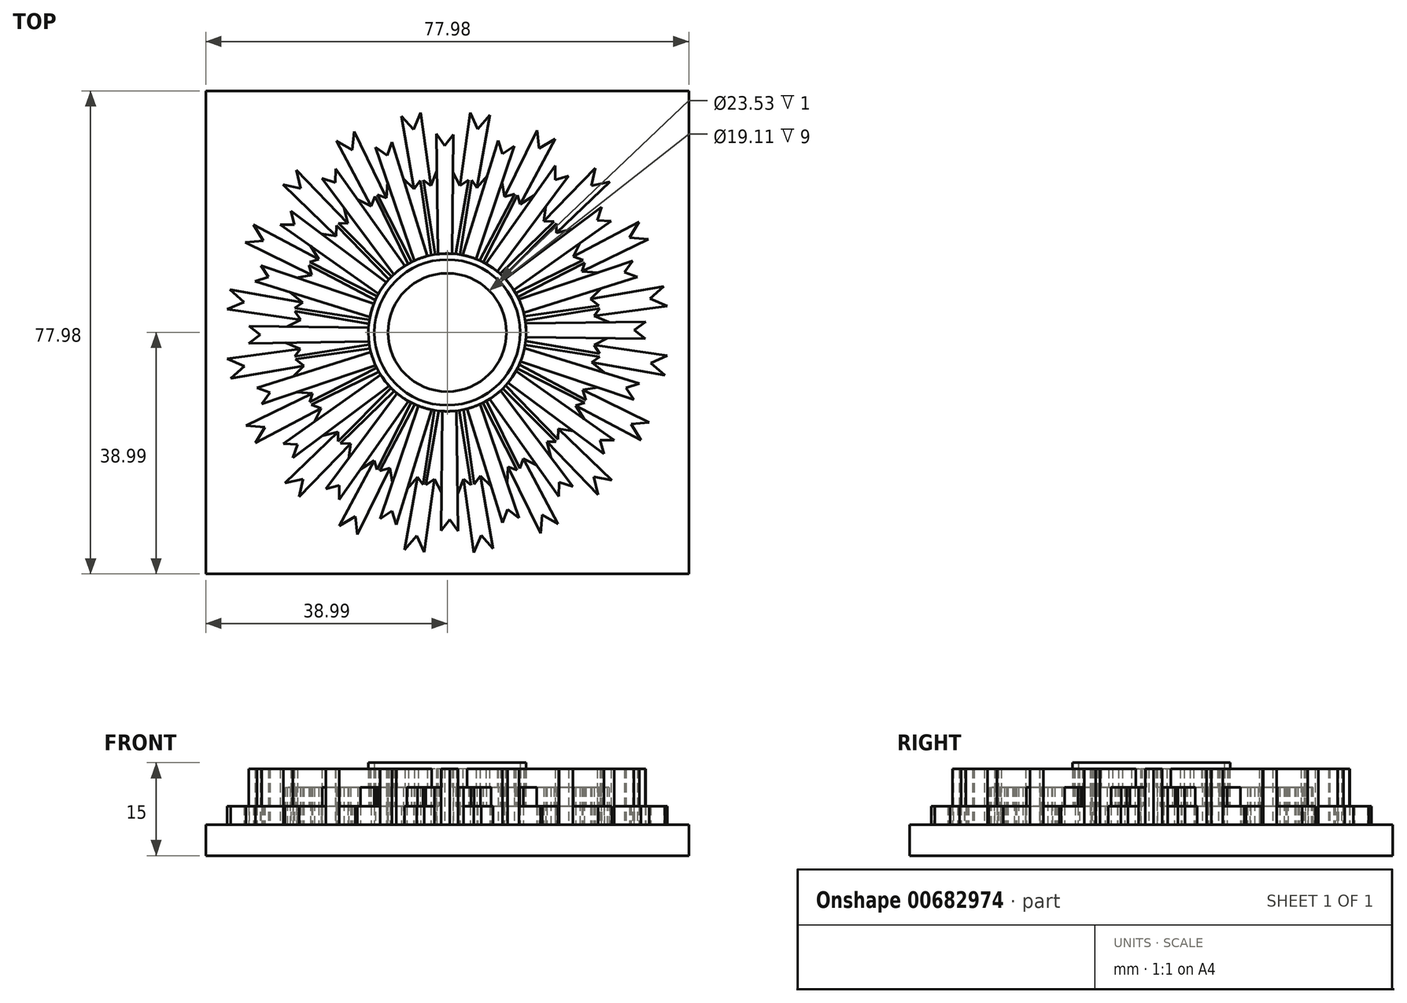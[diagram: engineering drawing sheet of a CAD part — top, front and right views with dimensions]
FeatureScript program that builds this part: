
annotation { "Feature Type Name" : "Feature", "Feature Type Description" : "" }
export const myFeature = defineFeature(function(context is Context, id is Id, definition is map)
    precondition{}
    {
        {
            var Q0;
            Q0=qCreatedBy(makeId("Top.planeOp"),FACE);
            var sketch = newSketch(context, id + "F0", { "sketchPlane" : qUnion([Q0])});
            skCircle(sketch, "E0", {"center": v(0, 0) * mm, "radius": 9.55 * mm});
            skCircle(sketch, "E1", {"center": v(0, 0) * mm, "radius": 11.77 * mm});
            skCircle(sketch, "E2", {"center": v(0, 0) * mm, "radius": 12.74 * mm});
            skLineSegment(sketch, "E3", {"start": v(-8.1, -9.83) * mm, "end": v(-19.6, -25.28) * mm});
            skLineSegment(sketch, "E4", {"start": v(-19.6, -25.28) * mm, "end": v(-17.42, -24.67) * mm});
            skLineSegment(sketch, "E5", {"start": v(-17.42, -24.67) * mm, "end": v(-17.42, -26.96) * mm});
            skLineSegment(sketch, "E6", {"start": v(-17.42, -26.96) * mm, "end": v(-6.24, -11.1) * mm});
            skLineSegment(sketch, "E7.1.0", {"start": v(-8.24, -31.02) * mm, "end": v(-2.5, -12.49) * mm});
            skLineSegment(sketch, "E7.1.1", {"start": v(-8.95, -28.84) * mm, "end": v(-8.24, -31.02) * mm});
            skLineSegment(sketch, "E7.1.2", {"start": v(-10.83, -30.1) * mm, "end": v(-8.95, -28.84) * mm});
            skLineSegment(sketch, "E7.1.3", {"start": v(-4.67, -11.85) * mm, "end": v(-10.83, -30.1) * mm});
            skLineSegment(sketch, "E7.2.0", {"start": v(1.75, -32.05) * mm, "end": v(1.47, -12.65) * mm});
            skLineSegment(sketch, "E7.2.1", {"start": v(0.4, -30.2) * mm, "end": v(1.75, -32.05) * mm});
            skLineSegment(sketch, "E7.2.2", {"start": v(-1, -31.97) * mm, "end": v(0.4, -30.2) * mm});
            skLineSegment(sketch, "E7.2.3", {"start": v(-0.77, -12.71) * mm, "end": v(-1, -31.97) * mm});
            skLineSegment(sketch, "E7.3.0", {"start": v(11.57, -29.94) * mm, "end": v(5.31, -11.58) * mm});
            skLineSegment(sketch, "E7.3.1", {"start": v(9.71, -28.6) * mm, "end": v(11.57, -29.94) * mm});
            skLineSegment(sketch, "E7.3.2", {"start": v(8.93, -30.71) * mm, "end": v(9.71, -28.6) * mm});
            skLineSegment(sketch, "E7.3.3", {"start": v(3.2, -12.33) * mm, "end": v(8.93, -30.71) * mm});
            skLineSegment(sketch, "E7.4.0", {"start": v(20.25, -24.9) * mm, "end": v(8.63, -9.37) * mm});
            skLineSegment(sketch, "E7.4.1", {"start": v(18.08, -24.2) * mm, "end": v(20.25, -24.9) * mm});
            skLineSegment(sketch, "E7.4.2", {"start": v(17.98, -26.45) * mm, "end": v(18.08, -24.2) * mm});
            skLineSegment(sketch, "E7.4.3", {"start": v(6.85, -10.74) * mm, "end": v(17.98, -26.45) * mm});
            skLineSegment(sketch, "E7.5.0", {"start": v(26.96, -17.42) * mm, "end": v(11.1, -6.24) * mm});
            skLineSegment(sketch, "E7.5.1", {"start": v(24.67, -17.42) * mm, "end": v(26.96, -17.42) * mm});
            skLineSegment(sketch, "E7.5.2", {"start": v(25.28, -19.6) * mm, "end": v(24.67, -17.42) * mm});
            skLineSegment(sketch, "E7.5.3", {"start": v(9.83, -8.1) * mm, "end": v(25.28, -19.6) * mm});
            skLineSegment(sketch, "E7.6.0", {"start": v(31.02, -8.24) * mm, "end": v(12.49, -2.5) * mm});
            skLineSegment(sketch, "E7.6.1", {"start": v(28.84, -8.95) * mm, "end": v(31.02, -8.24) * mm});
            skLineSegment(sketch, "E7.6.2", {"start": v(30.1, -10.83) * mm, "end": v(28.84, -8.95) * mm});
            skLineSegment(sketch, "E7.6.3", {"start": v(11.85, -4.67) * mm, "end": v(30.1, -10.83) * mm});
            skLineSegment(sketch, "E7.7.0", {"start": v(32.05, 1.75) * mm, "end": v(12.65, 1.47) * mm});
            skLineSegment(sketch, "E7.7.1", {"start": v(30.2, 0.4) * mm, "end": v(32.05, 1.75) * mm});
            skLineSegment(sketch, "E7.7.2", {"start": v(31.97, -1) * mm, "end": v(30.2, 0.4) * mm});
            skLineSegment(sketch, "E7.7.3", {"start": v(12.71, -0.77) * mm, "end": v(31.97, -1) * mm});
            skLineSegment(sketch, "E7.8.0", {"start": v(29.94, 11.57) * mm, "end": v(11.58, 5.31) * mm});
            skLineSegment(sketch, "E7.8.1", {"start": v(28.6, 9.71) * mm, "end": v(29.94, 11.57) * mm});
            skLineSegment(sketch, "E7.8.2", {"start": v(30.71, 8.93) * mm, "end": v(28.6, 9.71) * mm});
            skLineSegment(sketch, "E7.8.3", {"start": v(12.33, 3.2) * mm, "end": v(30.71, 8.93) * mm});
            skLineSegment(sketch, "E7.9.0", {"start": v(24.9, 20.25) * mm, "end": v(9.37, 8.63) * mm});
            skLineSegment(sketch, "E7.9.1", {"start": v(24.2, 18.08) * mm, "end": v(24.9, 20.25) * mm});
            skLineSegment(sketch, "E7.9.2", {"start": v(26.45, 17.98) * mm, "end": v(24.2, 18.08) * mm});
            skLineSegment(sketch, "E7.9.3", {"start": v(10.74, 6.85) * mm, "end": v(26.45, 17.98) * mm});
            skLineSegment(sketch, "E7.10.0", {"start": v(17.42, 26.96) * mm, "end": v(6.24, 11.1) * mm});
            skLineSegment(sketch, "E7.10.1", {"start": v(17.42, 24.67) * mm, "end": v(17.42, 26.96) * mm});
            skLineSegment(sketch, "E7.10.2", {"start": v(19.6, 25.28) * mm, "end": v(17.42, 24.67) * mm});
            skLineSegment(sketch, "E7.10.3", {"start": v(8.1, 9.83) * mm, "end": v(19.6, 25.28) * mm});
            skLineSegment(sketch, "E7.11.0", {"start": v(8.24, 31.02) * mm, "end": v(2.5, 12.49) * mm});
            skLineSegment(sketch, "E7.11.1", {"start": v(8.95, 28.84) * mm, "end": v(8.24, 31.02) * mm});
            skLineSegment(sketch, "E7.11.2", {"start": v(10.83, 30.1) * mm, "end": v(8.95, 28.84) * mm});
            skLineSegment(sketch, "E7.11.3", {"start": v(4.67, 11.85) * mm, "end": v(10.83, 30.1) * mm});
            skLineSegment(sketch, "E7.12.0", {"start": v(-1.75, 32.05) * mm, "end": v(-1.47, 12.65) * mm});
            skLineSegment(sketch, "E7.12.1", {"start": v(-0.4, 30.2) * mm, "end": v(-1.75, 32.05) * mm});
            skLineSegment(sketch, "E7.12.2", {"start": v(1, 31.97) * mm, "end": v(-0.4, 30.2) * mm});
            skLineSegment(sketch, "E7.12.3", {"start": v(0.77, 12.71) * mm, "end": v(1, 31.97) * mm});
            skLineSegment(sketch, "E7.13.0", {"start": v(-11.57, 29.94) * mm, "end": v(-5.31, 11.58) * mm});
            skLineSegment(sketch, "E7.13.1", {"start": v(-9.71, 28.6) * mm, "end": v(-11.57, 29.94) * mm});
            skLineSegment(sketch, "E7.13.2", {"start": v(-8.93, 30.71) * mm, "end": v(-9.71, 28.6) * mm});
            skLineSegment(sketch, "E7.13.3", {"start": v(-3.2, 12.33) * mm, "end": v(-8.93, 30.71) * mm});
            skLineSegment(sketch, "E7.14.0", {"start": v(-20.25, 24.9) * mm, "end": v(-8.63, 9.37) * mm});
            skLineSegment(sketch, "E7.14.1", {"start": v(-18.08, 24.2) * mm, "end": v(-20.25, 24.9) * mm});
            skLineSegment(sketch, "E7.14.2", {"start": v(-17.98, 26.45) * mm, "end": v(-18.08, 24.2) * mm});
            skLineSegment(sketch, "E7.14.3", {"start": v(-6.85, 10.74) * mm, "end": v(-17.98, 26.45) * mm});
            skLineSegment(sketch, "E7.15.0", {"start": v(-26.96, 17.42) * mm, "end": v(-11.1, 6.24) * mm});
            skLineSegment(sketch, "E7.15.1", {"start": v(-24.67, 17.42) * mm, "end": v(-26.96, 17.42) * mm});
            skLineSegment(sketch, "E7.15.2", {"start": v(-25.28, 19.6) * mm, "end": v(-24.67, 17.42) * mm});
            skLineSegment(sketch, "E7.15.3", {"start": v(-9.83, 8.1) * mm, "end": v(-25.28, 19.6) * mm});
            skLineSegment(sketch, "E7.16.0", {"start": v(-31.02, 8.24) * mm, "end": v(-12.49, 2.5) * mm});
            skLineSegment(sketch, "E7.16.1", {"start": v(-28.84, 8.95) * mm, "end": v(-31.02, 8.24) * mm});
            skLineSegment(sketch, "E7.16.2", {"start": v(-30.1, 10.83) * mm, "end": v(-28.84, 8.95) * mm});
            skLineSegment(sketch, "E7.16.3", {"start": v(-11.85, 4.67) * mm, "end": v(-30.1, 10.83) * mm});
            skLineSegment(sketch, "E7.17.0", {"start": v(-32.05, -1.75) * mm, "end": v(-12.65, -1.47) * mm});
            skLineSegment(sketch, "E7.17.1", {"start": v(-30.2, -0.4) * mm, "end": v(-32.05, -1.75) * mm});
            skLineSegment(sketch, "E7.17.2", {"start": v(-31.97, 1) * mm, "end": v(-30.2, -0.4) * mm});
            skLineSegment(sketch, "E7.17.3", {"start": v(-12.71, 0.77) * mm, "end": v(-31.97, 1) * mm});
            skLineSegment(sketch, "E7.18.0", {"start": v(-29.94, -11.57) * mm, "end": v(-11.58, -5.31) * mm});
            skLineSegment(sketch, "E7.18.1", {"start": v(-28.6, -9.71) * mm, "end": v(-29.94, -11.57) * mm});
            skLineSegment(sketch, "E7.18.2", {"start": v(-30.71, -8.93) * mm, "end": v(-28.6, -9.71) * mm});
            skLineSegment(sketch, "E7.18.3", {"start": v(-12.33, -3.2) * mm, "end": v(-30.71, -8.93) * mm});
            skLineSegment(sketch, "E7.19.0", {"start": v(-24.9, -20.25) * mm, "end": v(-9.37, -8.63) * mm});
            skLineSegment(sketch, "E7.19.1", {"start": v(-24.2, -18.08) * mm, "end": v(-24.9, -20.25) * mm});
            skLineSegment(sketch, "E7.19.2", {"start": v(-26.45, -17.98) * mm, "end": v(-24.2, -18.08) * mm});
            skLineSegment(sketch, "E7.19.3", {"start": v(-10.74, -6.85) * mm, "end": v(-26.45, -17.98) * mm});
            skLineSegment(sketch, "E8", {"start": v(-14, -22.1) * mm, "end": v(-11.8, -20.73) * mm});
            skLineSegment(sketch, "E9", {"start": v(-11.8, -20.73) * mm, "end": v(-11.35, -22.17) * mm});
            skLineSegment(sketch, "E10", {"start": v(-11.35, -22.17) * mm, "end": v(-5.84, -11.32) * mm});
            skLineSegment(sketch, "E11", {"start": v(-5.22, -11.62) * mm, "end": v(-10.89, -22.36) * mm});
            skLineSegment(sketch, "E12", {"start": v(-10.89, -22.36) * mm, "end": v(-9.26, -21.9) * mm});
            skLineSegment(sketch, "E13", {"start": v(-9.26, -21.9) * mm, "end": v(-8.86, -24.28) * mm});
            skLineSegment(sketch, "E14", {"start": v(-11.8, -20.73) * mm, "end": v(-17.42, -31.26) * mm});
            skLineSegment(sketch, "E15", {"start": v(-17.42, -31.26) * mm, "end": v(-14.82, -29.7) * mm});
            skLineSegment(sketch, "E16", {"start": v(-14.82, -29.7) * mm, "end": v(-14.53, -32.63) * mm});
            skLineSegment(sketch, "E17", {"start": v(-14.53, -32.63) * mm, "end": v(-9.26, -21.9) * mm});
            skLineSegment(sketch, "E18.1.0", {"start": v(-6.49, -25.35) * mm, "end": v(-4.81, -23.36) * mm});
            skLineSegment(sketch, "E18.1.1", {"start": v(-4.81, -23.36) * mm, "end": v(-6.91, -35.11) * mm});
            skLineSegment(sketch, "E18.1.2", {"start": v(-4.81, -23.36) * mm, "end": v(-3.94, -24.6) * mm});
            skLineSegment(sketch, "E18.1.3", {"start": v(-3.94, -24.6) * mm, "end": v(-2.05, -12.57) * mm});
            skLineSegment(sketch, "E18.1.4", {"start": v(-3.74, -35.52) * mm, "end": v(-2.04, -23.68) * mm});
            skLineSegment(sketch, "E18.1.5", {"start": v(-3.45, -24.63) * mm, "end": v(-2.04, -23.68) * mm});
            skLineSegment(sketch, "E18.1.6", {"start": v(-1.37, -12.66) * mm, "end": v(-3.45, -24.63) * mm});
            skLineSegment(sketch, "E18.1.7", {"start": v(-2.04, -23.68) * mm, "end": v(-0.93, -25.83) * mm});
            skLineSegment(sketch, "E18.1.8", {"start": v(-4.92, -32.82) * mm, "end": v(-3.74, -35.52) * mm});
            skLineSegment(sketch, "E18.1.9", {"start": v(-6.91, -35.11) * mm, "end": v(-4.92, -32.82) * mm});
            skLineSegment(sketch, "E18.2.0", {"start": v(1.67, -26.11) * mm, "end": v(2.64, -23.7) * mm});
            skLineSegment(sketch, "E18.2.1", {"start": v(2.64, -23.7) * mm, "end": v(4.28, -35.53) * mm});
            skLineSegment(sketch, "E18.2.2", {"start": v(2.64, -23.7) * mm, "end": v(3.85, -24.6) * mm});
            skLineSegment(sketch, "E18.2.3", {"start": v(3.85, -24.6) * mm, "end": v(1.93, -12.59) * mm});
            skLineSegment(sketch, "E18.2.4", {"start": v(7.42, -34.94) * mm, "end": v(5.38, -23.16) * mm});
            skLineSegment(sketch, "E18.2.5", {"start": v(4.33, -24.49) * mm, "end": v(5.38, -23.16) * mm});
            skLineSegment(sketch, "E18.2.6", {"start": v(2.6, -12.47) * mm, "end": v(4.33, -24.49) * mm});
            skLineSegment(sketch, "E18.2.7", {"start": v(5.38, -23.16) * mm, "end": v(7.1, -24.85) * mm});
            skLineSegment(sketch, "E18.2.8", {"start": v(5.47, -32.74) * mm, "end": v(7.42, -34.94) * mm});
            skLineSegment(sketch, "E18.2.9", {"start": v(4.28, -35.53) * mm, "end": v(5.47, -32.74) * mm});
            skLineSegment(sketch, "E18.3.0", {"start": v(9.65, -24.32) * mm, "end": v(9.84, -21.72) * mm});
            skLineSegment(sketch, "E18.3.1", {"start": v(9.84, -21.72) * mm, "end": v(15.05, -32.47) * mm});
            skLineSegment(sketch, "E18.3.2", {"start": v(9.84, -21.72) * mm, "end": v(11.27, -22.21) * mm});
            skLineSegment(sketch, "E18.3.3", {"start": v(11.27, -22.21) * mm, "end": v(5.73, -11.38) * mm});
            skLineSegment(sketch, "E18.3.4", {"start": v(17.85, -30.93) * mm, "end": v(12.27, -20.36) * mm});
            skLineSegment(sketch, "E18.3.5", {"start": v(11.69, -21.95) * mm, "end": v(12.27, -20.36) * mm});
            skLineSegment(sketch, "E18.3.6", {"start": v(6.33, -11.05) * mm, "end": v(11.69, -21.95) * mm});
            skLineSegment(sketch, "E18.3.7", {"start": v(12.27, -20.36) * mm, "end": v(14.43, -21.44) * mm});
            skLineSegment(sketch, "E18.3.8", {"start": v(15.31, -29.45) * mm, "end": v(17.85, -30.93) * mm});
            skLineSegment(sketch, "E18.3.9", {"start": v(15.05, -32.47) * mm, "end": v(15.31, -29.45) * mm});
            skLineSegment(sketch, "E18.4.0", {"start": v(16.7, -20.15) * mm, "end": v(16.07, -17.62) * mm});
            skLineSegment(sketch, "E18.4.1", {"start": v(16.07, -17.62) * mm, "end": v(24.34, -26.23) * mm});
            skLineSegment(sketch, "E18.4.2", {"start": v(16.07, -17.62) * mm, "end": v(17.58, -17.64) * mm});
            skLineSegment(sketch, "E18.4.3", {"start": v(17.58, -17.64) * mm, "end": v(8.96, -9.05) * mm});
            skLineSegment(sketch, "E18.4.4", {"start": v(26.54, -23.9) * mm, "end": v(17.96, -15.57) * mm});
            skLineSegment(sketch, "E18.4.5", {"start": v(17.9, -17.27) * mm, "end": v(17.96, -15.57) * mm});
            skLineSegment(sketch, "E18.4.6", {"start": v(9.44, -8.55) * mm, "end": v(17.9, -17.27) * mm});
            skLineSegment(sketch, "E18.4.7", {"start": v(17.96, -15.57) * mm, "end": v(20.35, -15.93) * mm});
            skLineSegment(sketch, "E18.4.8", {"start": v(23.66, -23.27) * mm, "end": v(26.54, -23.9) * mm});
            skLineSegment(sketch, "E18.4.9", {"start": v(24.34, -26.23) * mm, "end": v(23.66, -23.27) * mm});
            skLineSegment(sketch, "E18.5.0", {"start": v(22.1, -14) * mm, "end": v(20.73, -11.8) * mm});
            skLineSegment(sketch, "E18.5.1", {"start": v(20.73, -11.8) * mm, "end": v(31.26, -17.42) * mm});
            skLineSegment(sketch, "E18.5.2", {"start": v(20.73, -11.8) * mm, "end": v(22.17, -11.35) * mm});
            skLineSegment(sketch, "E18.5.3", {"start": v(22.17, -11.35) * mm, "end": v(11.32, -5.84) * mm});
            skLineSegment(sketch, "E18.5.4", {"start": v(32.63, -14.53) * mm, "end": v(21.9, -9.26) * mm});
            skLineSegment(sketch, "E18.5.5", {"start": v(22.36, -10.89) * mm, "end": v(21.9, -9.26) * mm});
            skLineSegment(sketch, "E18.5.6", {"start": v(11.62, -5.22) * mm, "end": v(22.36, -10.89) * mm});
            skLineSegment(sketch, "E18.5.7", {"start": v(21.9, -9.26) * mm, "end": v(24.28, -8.86) * mm});
            skLineSegment(sketch, "E18.5.8", {"start": v(29.7, -14.82) * mm, "end": v(32.63, -14.53) * mm});
            skLineSegment(sketch, "E18.5.9", {"start": v(31.26, -17.42) * mm, "end": v(29.7, -14.82) * mm});
            skLineSegment(sketch, "E18.6.0", {"start": v(25.35, -6.49) * mm, "end": v(23.36, -4.81) * mm});
            skLineSegment(sketch, "E18.6.1", {"start": v(23.36, -4.81) * mm, "end": v(35.11, -6.91) * mm});
            skLineSegment(sketch, "E18.6.2", {"start": v(23.36, -4.81) * mm, "end": v(24.6, -3.94) * mm});
            skLineSegment(sketch, "E18.6.3", {"start": v(24.6, -3.94) * mm, "end": v(12.57, -2.05) * mm});
            skLineSegment(sketch, "E18.6.4", {"start": v(35.52, -3.74) * mm, "end": v(23.68, -2.04) * mm});
            skLineSegment(sketch, "E18.6.5", {"start": v(24.63, -3.45) * mm, "end": v(23.68, -2.04) * mm});
            skLineSegment(sketch, "E18.6.6", {"start": v(12.66, -1.37) * mm, "end": v(24.63, -3.45) * mm});
            skLineSegment(sketch, "E18.6.7", {"start": v(23.68, -2.04) * mm, "end": v(25.83, -0.93) * mm});
            skLineSegment(sketch, "E18.6.8", {"start": v(32.82, -4.92) * mm, "end": v(35.52, -3.74) * mm});
            skLineSegment(sketch, "E18.6.9", {"start": v(35.11, -6.91) * mm, "end": v(32.82, -4.92) * mm});
            skLineSegment(sketch, "E18.7.0", {"start": v(26.11, 1.67) * mm, "end": v(23.7, 2.64) * mm});
            skLineSegment(sketch, "E18.7.1", {"start": v(23.7, 2.64) * mm, "end": v(35.53, 4.28) * mm});
            skLineSegment(sketch, "E18.7.2", {"start": v(23.7, 2.64) * mm, "end": v(24.6, 3.85) * mm});
            skLineSegment(sketch, "E18.7.3", {"start": v(24.6, 3.85) * mm, "end": v(12.59, 1.93) * mm});
            skLineSegment(sketch, "E18.7.4", {"start": v(34.94, 7.42) * mm, "end": v(23.16, 5.38) * mm});
            skLineSegment(sketch, "E18.7.5", {"start": v(24.49, 4.33) * mm, "end": v(23.16, 5.38) * mm});
            skLineSegment(sketch, "E18.7.6", {"start": v(12.47, 2.6) * mm, "end": v(24.49, 4.33) * mm});
            skLineSegment(sketch, "E18.7.7", {"start": v(23.16, 5.38) * mm, "end": v(24.85, 7.1) * mm});
            skLineSegment(sketch, "E18.7.8", {"start": v(32.74, 5.47) * mm, "end": v(34.94, 7.42) * mm});
            skLineSegment(sketch, "E18.7.9", {"start": v(35.53, 4.28) * mm, "end": v(32.74, 5.47) * mm});
            skLineSegment(sketch, "E18.8.0", {"start": v(24.32, 9.65) * mm, "end": v(21.72, 9.84) * mm});
            skLineSegment(sketch, "E18.8.1", {"start": v(21.72, 9.84) * mm, "end": v(32.47, 15.05) * mm});
            skLineSegment(sketch, "E18.8.2", {"start": v(21.72, 9.84) * mm, "end": v(22.21, 11.27) * mm});
            skLineSegment(sketch, "E18.8.3", {"start": v(22.21, 11.27) * mm, "end": v(11.38, 5.73) * mm});
            skLineSegment(sketch, "E18.8.4", {"start": v(30.93, 17.85) * mm, "end": v(20.36, 12.27) * mm});
            skLineSegment(sketch, "E18.8.5", {"start": v(21.95, 11.69) * mm, "end": v(20.36, 12.27) * mm});
            skLineSegment(sketch, "E18.8.6", {"start": v(11.05, 6.33) * mm, "end": v(21.95, 11.69) * mm});
            skLineSegment(sketch, "E18.8.7", {"start": v(20.36, 12.27) * mm, "end": v(21.44, 14.43) * mm});
            skLineSegment(sketch, "E18.8.8", {"start": v(29.45, 15.31) * mm, "end": v(30.93, 17.85) * mm});
            skLineSegment(sketch, "E18.8.9", {"start": v(32.47, 15.05) * mm, "end": v(29.45, 15.31) * mm});
            skLineSegment(sketch, "E18.9.0", {"start": v(20.15, 16.7) * mm, "end": v(17.62, 16.07) * mm});
            skLineSegment(sketch, "E18.9.1", {"start": v(17.62, 16.07) * mm, "end": v(26.23, 24.34) * mm});
            skLineSegment(sketch, "E18.9.2", {"start": v(17.62, 16.07) * mm, "end": v(17.64, 17.58) * mm});
            skLineSegment(sketch, "E18.9.3", {"start": v(17.64, 17.58) * mm, "end": v(9.05, 8.96) * mm});
            skLineSegment(sketch, "E18.9.4", {"start": v(23.9, 26.54) * mm, "end": v(15.57, 17.96) * mm});
            skLineSegment(sketch, "E18.9.5", {"start": v(17.27, 17.9) * mm, "end": v(15.57, 17.96) * mm});
            skLineSegment(sketch, "E18.9.6", {"start": v(8.55, 9.44) * mm, "end": v(17.27, 17.9) * mm});
            skLineSegment(sketch, "E18.9.7", {"start": v(15.57, 17.96) * mm, "end": v(15.93, 20.35) * mm});
            skLineSegment(sketch, "E18.9.8", {"start": v(23.27, 23.66) * mm, "end": v(23.9, 26.54) * mm});
            skLineSegment(sketch, "E18.9.9", {"start": v(26.23, 24.34) * mm, "end": v(23.27, 23.66) * mm});
            skLineSegment(sketch, "E18.10.0", {"start": v(14, 22.1) * mm, "end": v(11.8, 20.73) * mm});
            skLineSegment(sketch, "E18.10.1", {"start": v(11.8, 20.73) * mm, "end": v(17.42, 31.26) * mm});
            skLineSegment(sketch, "E18.10.2", {"start": v(11.8, 20.73) * mm, "end": v(11.35, 22.17) * mm});
            skLineSegment(sketch, "E18.10.3", {"start": v(11.35, 22.17) * mm, "end": v(5.84, 11.32) * mm});
            skLineSegment(sketch, "E18.10.4", {"start": v(14.53, 32.63) * mm, "end": v(9.26, 21.9) * mm});
            skLineSegment(sketch, "E18.10.5", {"start": v(10.89, 22.36) * mm, "end": v(9.26, 21.9) * mm});
            skLineSegment(sketch, "E18.10.6", {"start": v(5.22, 11.62) * mm, "end": v(10.89, 22.36) * mm});
            skLineSegment(sketch, "E18.10.7", {"start": v(9.26, 21.9) * mm, "end": v(8.86, 24.28) * mm});
            skLineSegment(sketch, "E18.10.8", {"start": v(14.82, 29.7) * mm, "end": v(14.53, 32.63) * mm});
            skLineSegment(sketch, "E18.10.9", {"start": v(17.42, 31.26) * mm, "end": v(14.82, 29.7) * mm});
            skLineSegment(sketch, "E18.11.0", {"start": v(6.49, 25.35) * mm, "end": v(4.81, 23.36) * mm});
            skLineSegment(sketch, "E18.11.1", {"start": v(4.81, 23.36) * mm, "end": v(6.91, 35.11) * mm});
            skLineSegment(sketch, "E18.11.2", {"start": v(4.81, 23.36) * mm, "end": v(3.94, 24.6) * mm});
            skLineSegment(sketch, "E18.11.3", {"start": v(3.94, 24.6) * mm, "end": v(2.05, 12.57) * mm});
            skLineSegment(sketch, "E18.11.4", {"start": v(3.74, 35.52) * mm, "end": v(2.04, 23.68) * mm});
            skLineSegment(sketch, "E18.11.5", {"start": v(3.45, 24.63) * mm, "end": v(2.04, 23.68) * mm});
            skLineSegment(sketch, "E18.11.6", {"start": v(1.37, 12.66) * mm, "end": v(3.45, 24.63) * mm});
            skLineSegment(sketch, "E18.11.7", {"start": v(2.04, 23.68) * mm, "end": v(0.93, 25.83) * mm});
            skLineSegment(sketch, "E18.11.8", {"start": v(4.92, 32.82) * mm, "end": v(3.74, 35.52) * mm});
            skLineSegment(sketch, "E18.11.9", {"start": v(6.91, 35.11) * mm, "end": v(4.92, 32.82) * mm});
            skLineSegment(sketch, "E18.12.0", {"start": v(-1.67, 26.11) * mm, "end": v(-2.64, 23.7) * mm});
            skLineSegment(sketch, "E18.12.1", {"start": v(-2.64, 23.7) * mm, "end": v(-4.28, 35.53) * mm});
            skLineSegment(sketch, "E18.12.2", {"start": v(-2.64, 23.7) * mm, "end": v(-3.85, 24.6) * mm});
            skLineSegment(sketch, "E18.12.3", {"start": v(-3.85, 24.6) * mm, "end": v(-1.93, 12.59) * mm});
            skLineSegment(sketch, "E18.12.4", {"start": v(-7.42, 34.94) * mm, "end": v(-5.38, 23.16) * mm});
            skLineSegment(sketch, "E18.12.5", {"start": v(-4.33, 24.49) * mm, "end": v(-5.38, 23.16) * mm});
            skLineSegment(sketch, "E18.12.6", {"start": v(-2.6, 12.47) * mm, "end": v(-4.33, 24.49) * mm});
            skLineSegment(sketch, "E18.12.7", {"start": v(-5.38, 23.16) * mm, "end": v(-7.1, 24.85) * mm});
            skLineSegment(sketch, "E18.12.8", {"start": v(-5.47, 32.74) * mm, "end": v(-7.42, 34.94) * mm});
            skLineSegment(sketch, "E18.12.9", {"start": v(-4.28, 35.53) * mm, "end": v(-5.47, 32.74) * mm});
            skLineSegment(sketch, "E18.13.0", {"start": v(-9.65, 24.32) * mm, "end": v(-9.84, 21.72) * mm});
            skLineSegment(sketch, "E18.13.1", {"start": v(-9.84, 21.72) * mm, "end": v(-15.05, 32.47) * mm});
            skLineSegment(sketch, "E18.13.2", {"start": v(-9.84, 21.72) * mm, "end": v(-11.27, 22.21) * mm});
            skLineSegment(sketch, "E18.13.3", {"start": v(-11.27, 22.21) * mm, "end": v(-5.73, 11.38) * mm});
            skLineSegment(sketch, "E18.13.4", {"start": v(-17.85, 30.93) * mm, "end": v(-12.27, 20.36) * mm});
            skLineSegment(sketch, "E18.13.5", {"start": v(-11.69, 21.95) * mm, "end": v(-12.27, 20.36) * mm});
            skLineSegment(sketch, "E18.13.6", {"start": v(-6.33, 11.05) * mm, "end": v(-11.69, 21.95) * mm});
            skLineSegment(sketch, "E18.13.7", {"start": v(-12.27, 20.36) * mm, "end": v(-14.43, 21.44) * mm});
            skLineSegment(sketch, "E18.13.8", {"start": v(-15.31, 29.45) * mm, "end": v(-17.85, 30.93) * mm});
            skLineSegment(sketch, "E18.13.9", {"start": v(-15.05, 32.47) * mm, "end": v(-15.31, 29.45) * mm});
            skLineSegment(sketch, "E18.14.0", {"start": v(-16.7, 20.15) * mm, "end": v(-16.07, 17.62) * mm});
            skLineSegment(sketch, "E18.14.1", {"start": v(-16.07, 17.62) * mm, "end": v(-24.34, 26.23) * mm});
            skLineSegment(sketch, "E18.14.2", {"start": v(-16.07, 17.62) * mm, "end": v(-17.58, 17.64) * mm});
            skLineSegment(sketch, "E18.14.3", {"start": v(-17.58, 17.64) * mm, "end": v(-8.96, 9.05) * mm});
            skLineSegment(sketch, "E18.14.4", {"start": v(-26.54, 23.9) * mm, "end": v(-17.96, 15.57) * mm});
            skLineSegment(sketch, "E18.14.5", {"start": v(-17.9, 17.27) * mm, "end": v(-17.96, 15.57) * mm});
            skLineSegment(sketch, "E18.14.6", {"start": v(-9.44, 8.55) * mm, "end": v(-17.9, 17.27) * mm});
            skLineSegment(sketch, "E18.14.7", {"start": v(-17.96, 15.57) * mm, "end": v(-20.35, 15.93) * mm});
            skLineSegment(sketch, "E18.14.8", {"start": v(-23.66, 23.27) * mm, "end": v(-26.54, 23.9) * mm});
            skLineSegment(sketch, "E18.14.9", {"start": v(-24.34, 26.23) * mm, "end": v(-23.66, 23.27) * mm});
            skLineSegment(sketch, "E18.15.0", {"start": v(-22.1, 14) * mm, "end": v(-20.73, 11.8) * mm});
            skLineSegment(sketch, "E18.15.1", {"start": v(-20.73, 11.8) * mm, "end": v(-31.26, 17.42) * mm});
            skLineSegment(sketch, "E18.15.2", {"start": v(-20.73, 11.8) * mm, "end": v(-22.17, 11.35) * mm});
            skLineSegment(sketch, "E18.15.3", {"start": v(-22.17, 11.35) * mm, "end": v(-11.32, 5.84) * mm});
            skLineSegment(sketch, "E18.15.4", {"start": v(-32.63, 14.53) * mm, "end": v(-21.9, 9.26) * mm});
            skLineSegment(sketch, "E18.15.5", {"start": v(-22.36, 10.89) * mm, "end": v(-21.9, 9.26) * mm});
            skLineSegment(sketch, "E18.15.6", {"start": v(-11.62, 5.22) * mm, "end": v(-22.36, 10.89) * mm});
            skLineSegment(sketch, "E18.15.7", {"start": v(-21.9, 9.26) * mm, "end": v(-24.28, 8.86) * mm});
            skLineSegment(sketch, "E18.15.8", {"start": v(-29.7, 14.82) * mm, "end": v(-32.63, 14.53) * mm});
            skLineSegment(sketch, "E18.15.9", {"start": v(-31.26, 17.42) * mm, "end": v(-29.7, 14.82) * mm});
            skLineSegment(sketch, "E18.16.0", {"start": v(-25.35, 6.49) * mm, "end": v(-23.36, 4.81) * mm});
            skLineSegment(sketch, "E18.16.1", {"start": v(-23.36, 4.81) * mm, "end": v(-35.11, 6.91) * mm});
            skLineSegment(sketch, "E18.16.2", {"start": v(-23.36, 4.81) * mm, "end": v(-24.6, 3.94) * mm});
            skLineSegment(sketch, "E18.16.3", {"start": v(-24.6, 3.94) * mm, "end": v(-12.57, 2.05) * mm});
            skLineSegment(sketch, "E18.16.4", {"start": v(-35.52, 3.74) * mm, "end": v(-23.68, 2.04) * mm});
            skLineSegment(sketch, "E18.16.5", {"start": v(-24.63, 3.45) * mm, "end": v(-23.68, 2.04) * mm});
            skLineSegment(sketch, "E18.16.6", {"start": v(-12.66, 1.37) * mm, "end": v(-24.63, 3.45) * mm});
            skLineSegment(sketch, "E18.16.7", {"start": v(-23.68, 2.04) * mm, "end": v(-25.83, 0.93) * mm});
            skLineSegment(sketch, "E18.16.8", {"start": v(-32.82, 4.92) * mm, "end": v(-35.52, 3.74) * mm});
            skLineSegment(sketch, "E18.16.9", {"start": v(-35.11, 6.91) * mm, "end": v(-32.82, 4.92) * mm});
            skLineSegment(sketch, "E18.17.0", {"start": v(-26.11, -1.67) * mm, "end": v(-23.7, -2.64) * mm});
            skLineSegment(sketch, "E18.17.1", {"start": v(-23.7, -2.64) * mm, "end": v(-35.53, -4.28) * mm});
            skLineSegment(sketch, "E18.17.2", {"start": v(-23.7, -2.64) * mm, "end": v(-24.6, -3.85) * mm});
            skLineSegment(sketch, "E18.17.3", {"start": v(-24.6, -3.85) * mm, "end": v(-12.59, -1.93) * mm});
            skLineSegment(sketch, "E18.17.4", {"start": v(-34.94, -7.42) * mm, "end": v(-23.16, -5.38) * mm});
            skLineSegment(sketch, "E18.17.5", {"start": v(-24.49, -4.33) * mm, "end": v(-23.16, -5.38) * mm});
            skLineSegment(sketch, "E18.17.6", {"start": v(-12.47, -2.6) * mm, "end": v(-24.49, -4.33) * mm});
            skLineSegment(sketch, "E18.17.7", {"start": v(-23.16, -5.38) * mm, "end": v(-24.85, -7.1) * mm});
            skLineSegment(sketch, "E18.17.8", {"start": v(-32.74, -5.47) * mm, "end": v(-34.94, -7.42) * mm});
            skLineSegment(sketch, "E18.17.9", {"start": v(-35.53, -4.28) * mm, "end": v(-32.74, -5.47) * mm});
            skLineSegment(sketch, "E18.18.0", {"start": v(-24.32, -9.65) * mm, "end": v(-21.72, -9.84) * mm});
            skLineSegment(sketch, "E18.18.1", {"start": v(-21.72, -9.84) * mm, "end": v(-32.47, -15.05) * mm});
            skLineSegment(sketch, "E18.18.2", {"start": v(-21.72, -9.84) * mm, "end": v(-22.21, -11.27) * mm});
            skLineSegment(sketch, "E18.18.3", {"start": v(-22.21, -11.27) * mm, "end": v(-11.38, -5.73) * mm});
            skLineSegment(sketch, "E18.18.4", {"start": v(-30.93, -17.85) * mm, "end": v(-20.36, -12.27) * mm});
            skLineSegment(sketch, "E18.18.5", {"start": v(-21.95, -11.69) * mm, "end": v(-20.36, -12.27) * mm});
            skLineSegment(sketch, "E18.18.6", {"start": v(-11.05, -6.33) * mm, "end": v(-21.95, -11.69) * mm});
            skLineSegment(sketch, "E18.18.7", {"start": v(-20.36, -12.27) * mm, "end": v(-21.44, -14.43) * mm});
            skLineSegment(sketch, "E18.18.8", {"start": v(-29.45, -15.31) * mm, "end": v(-30.93, -17.85) * mm});
            skLineSegment(sketch, "E18.18.9", {"start": v(-32.47, -15.05) * mm, "end": v(-29.45, -15.31) * mm});
            skLineSegment(sketch, "E18.19.0", {"start": v(-20.15, -16.7) * mm, "end": v(-17.62, -16.07) * mm});
            skLineSegment(sketch, "E18.19.1", {"start": v(-17.62, -16.07) * mm, "end": v(-26.23, -24.34) * mm});
            skLineSegment(sketch, "E18.19.2", {"start": v(-17.62, -16.07) * mm, "end": v(-17.64, -17.58) * mm});
            skLineSegment(sketch, "E18.19.3", {"start": v(-17.64, -17.58) * mm, "end": v(-9.05, -8.96) * mm});
            skLineSegment(sketch, "E18.19.4", {"start": v(-23.9, -26.54) * mm, "end": v(-15.57, -17.96) * mm});
            skLineSegment(sketch, "E18.19.5", {"start": v(-17.27, -17.9) * mm, "end": v(-15.57, -17.96) * mm});
            skLineSegment(sketch, "E18.19.6", {"start": v(-8.55, -9.44) * mm, "end": v(-17.27, -17.9) * mm});
            skLineSegment(sketch, "E18.19.7", {"start": v(-15.57, -17.96) * mm, "end": v(-15.93, -20.35) * mm});
            skLineSegment(sketch, "E18.19.8", {"start": v(-23.27, -23.66) * mm, "end": v(-23.9, -26.54) * mm});
            skLineSegment(sketch, "E18.19.9", {"start": v(-26.23, -24.34) * mm, "end": v(-23.27, -23.66) * mm});
            skLineSegment(sketch, "E19.bottom", {"start": v(39.23, 39.23) * mm, "end": v(-39.23, 39.23) * mm});
            skLineSegment(sketch, "E19.top", {"start": v(39.23, -39.23) * mm, "end": v(-39.23, -39.23) * mm});
            skLineSegment(sketch, "E19.left", {"start": v(39.23, 39.23) * mm, "end": v(39.23, -39.23) * mm});
            skLineSegment(sketch, "E19.right", {"start": v(-39.23, 39.23) * mm, "end": v(-39.23, -39.23) * mm});
            skSolve(sketch);
        }
        {
            var Q0;
            {var subQ64=sQuery(id+"F0.wireOp",EDGE,"E4");Q0=makeQuery(id+"F0.imprint","IMPRINT",FACE,{"disambiguationData":[TD([[makeQuery(id+"F0.imprint","IMPRINT",EDGE,{"derivedFrom":subQ64}),-1.0]])]});}
            var sketch = newSketch(context, id + "F1", { "sketchPlane" : qUnion([Q0])});
            skLineSegment(sketch, "E20.bottom", {"start": v(-38.99, -38.99) * mm, "end": v(38.99, -38.99) * mm});
            skLineSegment(sketch, "E20.top", {"start": v(-38.99, 38.99) * mm, "end": v(38.99, 38.99) * mm});
            skLineSegment(sketch, "E20.left", {"start": v(-38.99, -38.99) * mm, "end": v(-38.99, 38.99) * mm});
            skLineSegment(sketch, "E20.right", {"start": v(38.99, -38.99) * mm, "end": v(38.99, 38.99) * mm});
            skPoint(sketch, "E20.middle", {"position": v(0, 0) * mm});
            skPoint(sketch, "E21.middle", {"position": v(-38.99, -38.99) * mm});
            skSolve(sketch);
        }
        {
            var Q0;
            Q0 = qSketchRegion(id + "F1", true);
            extrude(context, id + "F2", {"entities" : qUnion([Q0]), "oppositeDirection" : true, "depth" : 5 * mm, "offsetDistance" : 25 * mm});
        }
        {
            var Q0;
            Q0=makeQuery(id+"F0.imprint","IMPRINT",FACE,{"disambiguationData":[TD([[makeQuery(id+"F0.imprint","IMPRINT",EDGE,{"derivedFrom":sQuery(id+"F0.wireOp",EDGE,"E18.2.1")}),1.0]])]});
            var Q1;
            Q1=makeQuery(id+"F0.imprint","IMPRINT",FACE,{"disambiguationData":[TD([[makeQuery(id+"F0.imprint","IMPRINT",EDGE,{"derivedFrom":sQuery(id+"F0.wireOp",EDGE,"E18.3.1")}),1.0]])]});
            var Q2;
            Q2=makeQuery(id+"F0.imprint","IMPRINT",FACE,{"disambiguationData":[TD([[makeQuery(id+"F0.imprint","IMPRINT",EDGE,{"derivedFrom":sQuery(id+"F0.wireOp",EDGE,"E18.4.1")}),1.0]])]});
            var Q3;
            Q3=makeQuery(id+"F0.imprint","IMPRINT",FACE,{"disambiguationData":[TD([[makeQuery(id+"F0.imprint","IMPRINT",EDGE,{"derivedFrom":sQuery(id+"F0.wireOp",EDGE,"E18.5.1")}),1.0]])]});
            var Q4;
            Q4=makeQuery(id+"F0.imprint","IMPRINT",FACE,{"disambiguationData":[TD([[makeQuery(id+"F0.imprint","IMPRINT",EDGE,{"derivedFrom":sQuery(id+"F0.wireOp",EDGE,"E18.6.1")}),1.0]])]});
            var Q5;
            Q5=makeQuery(id+"F0.imprint","IMPRINT",FACE,{"disambiguationData":[TD([[makeQuery(id+"F0.imprint","IMPRINT",EDGE,{"derivedFrom":sQuery(id+"F0.wireOp",EDGE,"E18.7.1")}),1.0]])]});
            var Q6;
            Q6=makeQuery(id+"F0.imprint","IMPRINT",FACE,{"disambiguationData":[TD([[makeQuery(id+"F0.imprint","IMPRINT",EDGE,{"derivedFrom":sQuery(id+"F0.wireOp",EDGE,"E18.8.1")}),1.0]])]});
            var Q7;
            Q7=makeQuery(id+"F0.imprint","IMPRINT",FACE,{"disambiguationData":[TD([[makeQuery(id+"F0.imprint","IMPRINT",EDGE,{"derivedFrom":sQuery(id+"F0.wireOp",EDGE,"E18.9.1")}),1.0]])]});
            var Q8;
            Q8=makeQuery(id+"F0.imprint","IMPRINT",FACE,{"disambiguationData":[TD([[makeQuery(id+"F0.imprint","IMPRINT",EDGE,{"derivedFrom":sQuery(id+"F0.wireOp",EDGE,"E18.10.1")}),1.0]])]});
            var Q9;
            Q9=makeQuery(id+"F0.imprint","IMPRINT",FACE,{"disambiguationData":[TD([[makeQuery(id+"F0.imprint","IMPRINT",EDGE,{"derivedFrom":sQuery(id+"F0.wireOp",EDGE,"E18.11.1")}),1.0]])]});
            var Q10;
            Q10=makeQuery(id+"F0.imprint","IMPRINT",FACE,{"disambiguationData":[TD([[makeQuery(id+"F0.imprint","IMPRINT",EDGE,{"derivedFrom":sQuery(id+"F0.wireOp",EDGE,"E18.12.1")}),1.0]])]});
            var Q11;
            Q11=makeQuery(id+"F0.imprint","IMPRINT",FACE,{"disambiguationData":[TD([[makeQuery(id+"F0.imprint","IMPRINT",EDGE,{"derivedFrom":sQuery(id+"F0.wireOp",EDGE,"E18.13.1")}),1.0]])]});
            var Q12;
            Q12=makeQuery(id+"F0.imprint","IMPRINT",FACE,{"disambiguationData":[TD([[makeQuery(id+"F0.imprint","IMPRINT",EDGE,{"derivedFrom":sQuery(id+"F0.wireOp",EDGE,"E18.14.1")}),1.0]])]});
            var Q13;
            Q13=makeQuery(id+"F0.imprint","IMPRINT",FACE,{"disambiguationData":[TD([[makeQuery(id+"F0.imprint","IMPRINT",EDGE,{"derivedFrom":sQuery(id+"F0.wireOp",EDGE,"E18.15.1")}),1.0]])]});
            var Q14;
            Q14=makeQuery(id+"F0.imprint","IMPRINT",FACE,{"disambiguationData":[TD([[makeQuery(id+"F0.imprint","IMPRINT",EDGE,{"derivedFrom":sQuery(id+"F0.wireOp",EDGE,"E18.16.1")}),1.0]])]});
            var Q15;
            Q15=makeQuery(id+"F0.imprint","IMPRINT",FACE,{"disambiguationData":[TD([[makeQuery(id+"F0.imprint","IMPRINT",EDGE,{"derivedFrom":sQuery(id+"F0.wireOp",EDGE,"E18.17.1")}),1.0]])]});
            var Q16;
            Q16=makeQuery(id+"F0.imprint","IMPRINT",FACE,{"disambiguationData":[TD([[makeQuery(id+"F0.imprint","IMPRINT",EDGE,{"derivedFrom":sQuery(id+"F0.wireOp",EDGE,"E18.18.1")}),1.0]])]});
            var Q17;
            Q17=makeQuery(id+"F0.imprint","IMPRINT",FACE,{"disambiguationData":[TD([[makeQuery(id+"F0.imprint","IMPRINT",EDGE,{"derivedFrom":sQuery(id+"F0.wireOp",EDGE,"E18.19.1")}),1.0]])]});
            var Q18;
            Q18=makeQuery(id+"F0.imprint","IMPRINT",FACE,{"disambiguationData":[TD([[makeQuery(id+"F0.imprint","IMPRINT",EDGE,{"derivedFrom":sQuery(id+"F0.wireOp",EDGE,"E9")}),-1.0]])]});
            var Q19;
            Q19=makeQuery(id+"F0.imprint","IMPRINT",FACE,{"disambiguationData":[TD([[makeQuery(id+"F0.imprint","IMPRINT",EDGE,{"derivedFrom":sQuery(id+"F0.wireOp",EDGE,"E18.1.1")}),1.0]])]});
            extrude(context, id + "F3", {"entities" : qUnion([Q0, Q1, Q2, Q3, Q4, Q5, Q6, Q7, Q8, Q9, Q10, Q11, Q12, Q13, Q14, Q15, Q16, Q17, Q18, Q19]), "operationType" : NewBodyOperationType.ADD, "depth" : 3 * mm, "offsetDistance" : 25 * mm});
        }
        {
            var Q0;
            {var subQ4=sQuery(id+"F0.wireOp",EDGE,"E18.13.0");Q0=makeQuery(id+"F0.imprint","IMPRINT",FACE,{"disambiguationData":[TD([[makeQuery(id+"F0.imprint","IMPRINT",EDGE,{"derivedFrom":subQ4}),1.0]])]});}
            var Q1;
            Q1=makeQuery(id+"F0.imprint","IMPRINT",FACE,{"disambiguationData":[TD([[makeQuery(id+"F0.imprint","IMPRINT",EDGE,{"derivedFrom":sQuery(id+"F0.wireOp",EDGE,"E18.13.5")}),1.0]])]});
            var Q2;
            {var subQ0=sQuery(id+"F0.wireOp",EDGE,"E18.14.0");Q2=makeQuery(id+"F0.imprint","IMPRINT",FACE,{"disambiguationData":[TD([[makeQuery(id+"F0.imprint","IMPRINT",EDGE,{"derivedFrom":subQ0}),1.0]])]});}
            var Q3;
            Q3=makeQuery(id+"F0.imprint","IMPRINT",FACE,{"disambiguationData":[TD([[makeQuery(id+"F0.imprint","IMPRINT",EDGE,{"derivedFrom":sQuery(id+"F0.wireOp",EDGE,"E18.14.5")}),1.0]])]});
            var Q4;
            {var subQ0=sQuery(id+"F0.wireOp",EDGE,"E18.15.0");Q4=makeQuery(id+"F0.imprint","IMPRINT",FACE,{"disambiguationData":[TD([[makeQuery(id+"F0.imprint","IMPRINT",EDGE,{"derivedFrom":subQ0}),1.0]])]});}
            var Q5;
            Q5=makeQuery(id+"F0.imprint","IMPRINT",FACE,{"disambiguationData":[TD([[makeQuery(id+"F0.imprint","IMPRINT",EDGE,{"derivedFrom":sQuery(id+"F0.wireOp",EDGE,"E18.15.5")}),1.0]])]});
            var Q6;
            {var subQ0=sQuery(id+"F0.wireOp",EDGE,"E18.16.0");Q6=makeQuery(id+"F0.imprint","IMPRINT",FACE,{"disambiguationData":[TD([[makeQuery(id+"F0.imprint","IMPRINT",EDGE,{"derivedFrom":subQ0}),1.0]])]});}
            var Q7;
            Q7=makeQuery(id+"F0.imprint","IMPRINT",FACE,{"disambiguationData":[TD([[makeQuery(id+"F0.imprint","IMPRINT",EDGE,{"derivedFrom":sQuery(id+"F0.wireOp",EDGE,"E18.16.5")}),1.0]])]});
            var Q8;
            {var subQ3=sQuery(id+"F0.wireOp",EDGE,"E18.17.0");Q8=makeQuery(id+"F0.imprint","IMPRINT",FACE,{"disambiguationData":[TD([[makeQuery(id+"F0.imprint","IMPRINT",EDGE,{"derivedFrom":subQ3}),1.0]])]});}
            var Q9;
            Q9=makeQuery(id+"F0.imprint","IMPRINT",FACE,{"disambiguationData":[TD([[makeQuery(id+"F0.imprint","IMPRINT",EDGE,{"derivedFrom":sQuery(id+"F0.wireOp",EDGE,"E18.17.5")}),1.0]])]});
            var Q10;
            {var subQ0=sQuery(id+"F0.wireOp",EDGE,"E18.18.0");Q10=makeQuery(id+"F0.imprint","IMPRINT",FACE,{"disambiguationData":[TD([[makeQuery(id+"F0.imprint","IMPRINT",EDGE,{"derivedFrom":subQ0}),1.0]])]});}
            var Q11;
            Q11=makeQuery(id+"F0.imprint","IMPRINT",FACE,{"disambiguationData":[TD([[makeQuery(id+"F0.imprint","IMPRINT",EDGE,{"derivedFrom":sQuery(id+"F0.wireOp",EDGE,"E18.18.5")}),1.0]])]});
            var Q12;
            {var subQ0=sQuery(id+"F0.wireOp",EDGE,"E18.19.0");Q12=makeQuery(id+"F0.imprint","IMPRINT",FACE,{"disambiguationData":[TD([[makeQuery(id+"F0.imprint","IMPRINT",EDGE,{"derivedFrom":subQ0}),1.0]])]});}
            var Q13;
            Q13=makeQuery(id+"F0.imprint","IMPRINT",FACE,{"disambiguationData":[TD([[makeQuery(id+"F0.imprint","IMPRINT",EDGE,{"derivedFrom":sQuery(id+"F0.wireOp",EDGE,"E18.19.5")}),1.0]])]});
            var Q14;
            {var subQ0=sQuery(id+"F0.wireOp",EDGE,"E8");Q14=makeQuery(id+"F0.imprint","IMPRINT",FACE,{"disambiguationData":[TD([[makeQuery(id+"F0.imprint","IMPRINT",EDGE,{"derivedFrom":subQ0}),1.0]])]});}
            var Q15;
            {var subQ0=sQuery(id+"F0.wireOp",EDGE,"E11");Q15=makeQuery(id+"F0.imprint","IMPRINT",FACE,{"disambiguationData":[TD([[makeQuery(id+"F0.imprint","IMPRINT",EDGE,{"derivedFrom":subQ0}),1.0]])]});}
            var Q16;
            {var subQ0=sQuery(id+"F0.wireOp",EDGE,"E18.1.0");Q16=makeQuery(id+"F0.imprint","IMPRINT",FACE,{"disambiguationData":[TD([[makeQuery(id+"F0.imprint","IMPRINT",EDGE,{"derivedFrom":subQ0}),1.0]])]});}
            var Q17;
            Q17=makeQuery(id+"F0.imprint","IMPRINT",FACE,{"disambiguationData":[TD([[makeQuery(id+"F0.imprint","IMPRINT",EDGE,{"derivedFrom":sQuery(id+"F0.wireOp",EDGE,"E18.1.5")}),1.0]])]});
            var Q18;
            {var subQ3=sQuery(id+"F0.wireOp",EDGE,"E18.2.0");Q18=makeQuery(id+"F0.imprint","IMPRINT",FACE,{"disambiguationData":[TD([[makeQuery(id+"F0.imprint","IMPRINT",EDGE,{"derivedFrom":subQ3}),1.0]])]});}
            var Q19;
            Q19=makeQuery(id+"F0.imprint","IMPRINT",FACE,{"disambiguationData":[TD([[makeQuery(id+"F0.imprint","IMPRINT",EDGE,{"derivedFrom":sQuery(id+"F0.wireOp",EDGE,"E18.2.5")}),1.0]])]});
            var Q20;
            {var subQ0=sQuery(id+"F0.wireOp",EDGE,"E18.3.0");Q20=makeQuery(id+"F0.imprint","IMPRINT",FACE,{"disambiguationData":[TD([[makeQuery(id+"F0.imprint","IMPRINT",EDGE,{"derivedFrom":subQ0}),1.0]])]});}
            var Q21;
            Q21=makeQuery(id+"F0.imprint","IMPRINT",FACE,{"disambiguationData":[TD([[makeQuery(id+"F0.imprint","IMPRINT",EDGE,{"derivedFrom":sQuery(id+"F0.wireOp",EDGE,"E18.3.5")}),1.0]])]});
            var Q22;
            {var subQ0=sQuery(id+"F0.wireOp",EDGE,"E18.4.0");Q22=makeQuery(id+"F0.imprint","IMPRINT",FACE,{"disambiguationData":[TD([[makeQuery(id+"F0.imprint","IMPRINT",EDGE,{"derivedFrom":subQ0}),1.0]])]});}
            var Q23;
            Q23=makeQuery(id+"F0.imprint","IMPRINT",FACE,{"disambiguationData":[TD([[makeQuery(id+"F0.imprint","IMPRINT",EDGE,{"derivedFrom":sQuery(id+"F0.wireOp",EDGE,"E18.4.5")}),1.0]])]});
            var Q24;
            {var subQ0=sQuery(id+"F0.wireOp",EDGE,"E18.5.0");Q24=makeQuery(id+"F0.imprint","IMPRINT",FACE,{"disambiguationData":[TD([[makeQuery(id+"F0.imprint","IMPRINT",EDGE,{"derivedFrom":subQ0}),1.0]])]});}
            var Q25;
            Q25=makeQuery(id+"F0.imprint","IMPRINT",FACE,{"disambiguationData":[TD([[makeQuery(id+"F0.imprint","IMPRINT",EDGE,{"derivedFrom":sQuery(id+"F0.wireOp",EDGE,"E18.5.5")}),1.0]])]});
            var Q26;
            {var subQ0=sQuery(id+"F0.wireOp",EDGE,"E18.6.0");Q26=makeQuery(id+"F0.imprint","IMPRINT",FACE,{"disambiguationData":[TD([[makeQuery(id+"F0.imprint","IMPRINT",EDGE,{"derivedFrom":subQ0}),1.0]])]});}
            var Q27;
            Q27=makeQuery(id+"F0.imprint","IMPRINT",FACE,{"disambiguationData":[TD([[makeQuery(id+"F0.imprint","IMPRINT",EDGE,{"derivedFrom":sQuery(id+"F0.wireOp",EDGE,"E18.6.5")}),1.0]])]});
            var Q28;
            {var subQ3=sQuery(id+"F0.wireOp",EDGE,"E18.7.0");Q28=makeQuery(id+"F0.imprint","IMPRINT",FACE,{"disambiguationData":[TD([[makeQuery(id+"F0.imprint","IMPRINT",EDGE,{"derivedFrom":subQ3}),1.0]])]});}
            var Q29;
            Q29=makeQuery(id+"F0.imprint","IMPRINT",FACE,{"disambiguationData":[TD([[makeQuery(id+"F0.imprint","IMPRINT",EDGE,{"derivedFrom":sQuery(id+"F0.wireOp",EDGE,"E18.7.5")}),1.0]])]});
            var Q30;
            {var subQ0=sQuery(id+"F0.wireOp",EDGE,"E18.8.0");Q30=makeQuery(id+"F0.imprint","IMPRINT",FACE,{"disambiguationData":[TD([[makeQuery(id+"F0.imprint","IMPRINT",EDGE,{"derivedFrom":subQ0}),1.0]])]});}
            var Q31;
            Q31=makeQuery(id+"F0.imprint","IMPRINT",FACE,{"disambiguationData":[TD([[makeQuery(id+"F0.imprint","IMPRINT",EDGE,{"derivedFrom":sQuery(id+"F0.wireOp",EDGE,"E18.8.5")}),1.0]])]});
            var Q32;
            {var subQ0=sQuery(id+"F0.wireOp",EDGE,"E18.9.0");Q32=makeQuery(id+"F0.imprint","IMPRINT",FACE,{"disambiguationData":[TD([[makeQuery(id+"F0.imprint","IMPRINT",EDGE,{"derivedFrom":subQ0}),1.0]])]});}
            var Q33;
            Q33=makeQuery(id+"F0.imprint","IMPRINT",FACE,{"disambiguationData":[TD([[makeQuery(id+"F0.imprint","IMPRINT",EDGE,{"derivedFrom":sQuery(id+"F0.wireOp",EDGE,"E18.9.5")}),1.0]])]});
            var Q34;
            {var subQ0=sQuery(id+"F0.wireOp",EDGE,"E18.10.0");Q34=makeQuery(id+"F0.imprint","IMPRINT",FACE,{"disambiguationData":[TD([[makeQuery(id+"F0.imprint","IMPRINT",EDGE,{"derivedFrom":subQ0}),1.0]])]});}
            var Q35;
            Q35=makeQuery(id+"F0.imprint","IMPRINT",FACE,{"disambiguationData":[TD([[makeQuery(id+"F0.imprint","IMPRINT",EDGE,{"derivedFrom":sQuery(id+"F0.wireOp",EDGE,"E18.10.5")}),1.0]])]});
            var Q36;
            {var subQ0=sQuery(id+"F0.wireOp",EDGE,"E18.11.0");Q36=makeQuery(id+"F0.imprint","IMPRINT",FACE,{"disambiguationData":[TD([[makeQuery(id+"F0.imprint","IMPRINT",EDGE,{"derivedFrom":subQ0}),1.0]])]});}
            var Q37;
            Q37=makeQuery(id+"F0.imprint","IMPRINT",FACE,{"disambiguationData":[TD([[makeQuery(id+"F0.imprint","IMPRINT",EDGE,{"derivedFrom":sQuery(id+"F0.wireOp",EDGE,"E18.11.5")}),1.0]])]});
            var Q38;
            {var subQ3=sQuery(id+"F0.wireOp",EDGE,"E18.12.0");Q38=makeQuery(id+"F0.imprint","IMPRINT",FACE,{"disambiguationData":[TD([[makeQuery(id+"F0.imprint","IMPRINT",EDGE,{"derivedFrom":subQ3}),1.0]])]});}
            var Q39;
            Q39=makeQuery(id+"F0.imprint","IMPRINT",FACE,{"disambiguationData":[TD([[makeQuery(id+"F0.imprint","IMPRINT",EDGE,{"derivedFrom":sQuery(id+"F0.wireOp",EDGE,"E18.12.5")}),1.0]])]});
            extrude(context, id + "F4", {"entities" : qUnion([Q0, Q1, Q2, Q3, Q4, Q5, Q6, Q7, Q8, Q9, Q10, Q11, Q12, Q13, Q14, Q15, Q16, Q17, Q18, Q19, Q20, Q21, Q22, Q23, Q24, Q25, Q26, Q27, Q28, Q29, Q30, Q31, Q32, Q33, Q34, Q35, Q36, Q37, Q38, Q39]), "operationType" : NewBodyOperationType.ADD, "depth" : 6 * mm, "offsetDistance" : 25 * mm});
        }
        {
            var Q0;
            {var subQ0=sQuery(id+"F0.wireOp",EDGE,"E7.15.1");Q0=makeQuery(id+"F0.imprint","IMPRINT",FACE,{"disambiguationData":[TD([[makeQuery(id+"F0.imprint","IMPRINT",EDGE,{"derivedFrom":subQ0}),1.0]])]});}
            var Q1;
            {var subQ0=sQuery(id+"F0.wireOp",EDGE,"E7.16.1");Q1=makeQuery(id+"F0.imprint","IMPRINT",FACE,{"disambiguationData":[TD([[makeQuery(id+"F0.imprint","IMPRINT",EDGE,{"derivedFrom":subQ0}),1.0]])]});}
            var Q2;
            {var subQ4=sQuery(id+"F0.wireOp",EDGE,"E7.17.1");Q2=makeQuery(id+"F0.imprint","IMPRINT",FACE,{"disambiguationData":[TD([[makeQuery(id+"F0.imprint","IMPRINT",EDGE,{"derivedFrom":subQ4}),1.0]])]});}
            var Q3;
            {var subQ0=sQuery(id+"F0.wireOp",EDGE,"E7.18.1");Q3=makeQuery(id+"F0.imprint","IMPRINT",FACE,{"disambiguationData":[TD([[makeQuery(id+"F0.imprint","IMPRINT",EDGE,{"derivedFrom":subQ0}),1.0]])]});}
            var Q4;
            {var subQ0=sQuery(id+"F0.wireOp",EDGE,"E7.19.1");Q4=makeQuery(id+"F0.imprint","IMPRINT",FACE,{"disambiguationData":[TD([[makeQuery(id+"F0.imprint","IMPRINT",EDGE,{"derivedFrom":subQ0}),1.0]])]});}
            var Q5;
            {var subQ0=sQuery(id+"F0.wireOp",EDGE,"E4");Q5=makeQuery(id+"F0.imprint","IMPRINT",FACE,{"disambiguationData":[TD([[makeQuery(id+"F0.imprint","IMPRINT",EDGE,{"derivedFrom":subQ0}),1.0]])]});}
            var Q6;
            {var subQ0=sQuery(id+"F0.wireOp",EDGE,"E7.1.1");Q6=makeQuery(id+"F0.imprint","IMPRINT",FACE,{"disambiguationData":[TD([[makeQuery(id+"F0.imprint","IMPRINT",EDGE,{"derivedFrom":subQ0}),1.0]])]});}
            var Q7;
            {var subQ4=sQuery(id+"F0.wireOp",EDGE,"E7.2.1");Q7=makeQuery(id+"F0.imprint","IMPRINT",FACE,{"disambiguationData":[TD([[makeQuery(id+"F0.imprint","IMPRINT",EDGE,{"derivedFrom":subQ4}),1.0]])]});}
            var Q8;
            {var subQ0=sQuery(id+"F0.wireOp",EDGE,"E7.3.1");Q8=makeQuery(id+"F0.imprint","IMPRINT",FACE,{"disambiguationData":[TD([[makeQuery(id+"F0.imprint","IMPRINT",EDGE,{"derivedFrom":subQ0}),1.0]])]});}
            var Q9;
            {var subQ0=sQuery(id+"F0.wireOp",EDGE,"E7.4.1");Q9=makeQuery(id+"F0.imprint","IMPRINT",FACE,{"disambiguationData":[TD([[makeQuery(id+"F0.imprint","IMPRINT",EDGE,{"derivedFrom":subQ0}),1.0]])]});}
            var Q10;
            {var subQ0=sQuery(id+"F0.wireOp",EDGE,"E7.5.1");Q10=makeQuery(id+"F0.imprint","IMPRINT",FACE,{"disambiguationData":[TD([[makeQuery(id+"F0.imprint","IMPRINT",EDGE,{"derivedFrom":subQ0}),1.0]])]});}
            var Q11;
            {var subQ0=sQuery(id+"F0.wireOp",EDGE,"E7.6.1");Q11=makeQuery(id+"F0.imprint","IMPRINT",FACE,{"disambiguationData":[TD([[makeQuery(id+"F0.imprint","IMPRINT",EDGE,{"derivedFrom":subQ0}),1.0]])]});}
            var Q12;
            {var subQ6=sQuery(id+"F0.wireOp",EDGE,"E7.7.1");Q12=makeQuery(id+"F0.imprint","IMPRINT",FACE,{"disambiguationData":[TD([[makeQuery(id+"F0.imprint","IMPRINT",EDGE,{"derivedFrom":subQ6}),1.0]])]});}
            var Q13;
            {var subQ0=sQuery(id+"F0.wireOp",EDGE,"E7.8.1");Q13=makeQuery(id+"F0.imprint","IMPRINT",FACE,{"disambiguationData":[TD([[makeQuery(id+"F0.imprint","IMPRINT",EDGE,{"derivedFrom":subQ0}),1.0]])]});}
            var Q14;
            {var subQ0=sQuery(id+"F0.wireOp",EDGE,"E7.9.1");Q14=makeQuery(id+"F0.imprint","IMPRINT",FACE,{"disambiguationData":[TD([[makeQuery(id+"F0.imprint","IMPRINT",EDGE,{"derivedFrom":subQ0}),1.0]])]});}
            var Q15;
            {var subQ0=sQuery(id+"F0.wireOp",EDGE,"E7.10.1");Q15=makeQuery(id+"F0.imprint","IMPRINT",FACE,{"disambiguationData":[TD([[makeQuery(id+"F0.imprint","IMPRINT",EDGE,{"derivedFrom":subQ0}),1.0]])]});}
            var Q16;
            {var subQ0=sQuery(id+"F0.wireOp",EDGE,"E7.11.1");Q16=makeQuery(id+"F0.imprint","IMPRINT",FACE,{"disambiguationData":[TD([[makeQuery(id+"F0.imprint","IMPRINT",EDGE,{"derivedFrom":subQ0}),1.0]])]});}
            var Q17;
            {var subQ4=sQuery(id+"F0.wireOp",EDGE,"E7.12.1");Q17=makeQuery(id+"F0.imprint","IMPRINT",FACE,{"disambiguationData":[TD([[makeQuery(id+"F0.imprint","IMPRINT",EDGE,{"derivedFrom":subQ4}),1.0]])]});}
            var Q18;
            {var subQ0=sQuery(id+"F0.wireOp",EDGE,"E7.13.1");Q18=makeQuery(id+"F0.imprint","IMPRINT",FACE,{"disambiguationData":[TD([[makeQuery(id+"F0.imprint","IMPRINT",EDGE,{"derivedFrom":subQ0}),1.0]])]});}
            var Q19;
            {var subQ0=sQuery(id+"F0.wireOp",EDGE,"E7.14.1");Q19=makeQuery(id+"F0.imprint","IMPRINT",FACE,{"disambiguationData":[TD([[makeQuery(id+"F0.imprint","IMPRINT",EDGE,{"derivedFrom":subQ0}),1.0]])]});}
            var Q20;
            Q20=makeQuery(id+"F0.imprint","IMPRINT",FACE,{"disambiguationData":[TD([[makeQuery(id+"F0.imprint","IMPRINT",EDGE,{"derivedFrom":sQuery(id+"F0.wireOp",EDGE,"E0")}),-1.0]])]});
            extrude(context, id + "F5", {"entities" : qUnion([Q0, Q1, Q2, Q3, Q4, Q5, Q6, Q7, Q8, Q9, Q10, Q11, Q12, Q13, Q14, Q15, Q16, Q17, Q18, Q19, Q20]), "operationType" : NewBodyOperationType.ADD, "depth" : 9 * mm, "offsetDistance" : 25 * mm});
        }
        {
            var Q0;
            Q0=makeQuery(id+"F0.imprint","IMPRINT",FACE,{"disambiguationData":[TD([[makeQuery(id+"F0.imprint","IMPRINT",EDGE,{"derivedFrom":sQuery(id+"F0.wireOp",EDGE,"E1")}),-1.0]])]});
            extrude(context, id + "F6", {"entities" : qUnion([Q0]), "operationType" : NewBodyOperationType.ADD, "depth" : 10 * mm, "offsetDistance" : 25 * mm});
        }
    });
